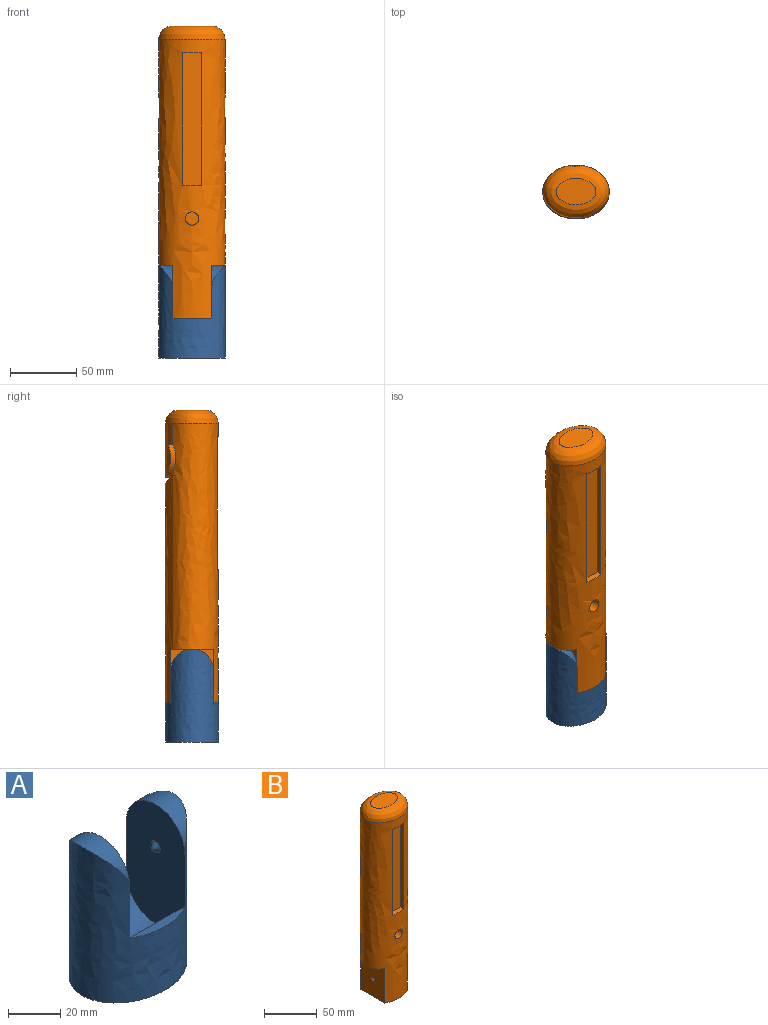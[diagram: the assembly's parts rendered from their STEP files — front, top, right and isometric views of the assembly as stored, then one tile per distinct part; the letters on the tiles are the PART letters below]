
ASSEMBLY  parts=2 mates=1
PART A: 13 faces, bbox 50x40x70 mm
  f0: extruded ~70x50mm, area 7085.2mm2, adj f1,f2,f3,f4,f5,f11,f12
  f1: plane 56x32mm, normal (1,0,0), area 1552.6mm2, adj f0,f6,f8,f12
  f2: plane 56x32mm, normal (-1,0,0), area 1552.6mm2, adj f0,f6,f10,f11
  f3: plane 30x4mm, normal (0,0,1), area 81.8mm2, adj f0,f6
  f4: plane 30x4mm, normal (0,0,1), area 81.8mm2, adj f0,f6
  f5: plane 50x40mm, normal (0,0,-1), area 1570.8mm2, adj f0
  f6: cylinder r=16mm len=32mm, axis (-1,0,0), area 1508mm2, adj f1,f2,f3,f4
  f7: plane 1x1mm, normal (1,0,0), area 0.8mm2, adj f8
  f8: cone r=0.5mm half-angle=45deg, axis (-1,0,0), area 26.7mm2, adj f1,f7
  f9: plane 1x1mm, normal (-1,0,0), area 0.8mm2, adj f10
  f10: cone r=0.5mm half-angle=45deg, axis (1,0,0), area 26.7mm2, adj f2,f9
  f11: cylinder r=16mm len=32mm, axis (-1,0,0), area 267.1mm2, adj f0,f2
  f12: cylinder r=16mm len=32mm, axis (1,0,0), area 267.1mm2, adj f0,f1
PART B: 30 faces, bbox 50.2x40.2x220.2 mm
  f0: extruded ~210x49.99mm, area 23499.3mm2, adj f1,f3,f4,f5,f6,f7,f8,f9
  f1: extruded ~40.83x32.29mm, area 960.6mm2, adj f0,f8,f21,f22,f23,f28
  f2: plane 30x20.01mm, normal (0,0,1), area 466.8mm2, adj f8
  f3: plane 32x10mm, normal (0,0,-1), area 223.6mm2, adj f0,f6
  f4: plane 32x10mm, normal (0,0,-1), area 223.6mm2, adj f0,f7
  f5: plane 40x30mm, normal (0,0,-1), area 1123.5mm2, adj f0,f6,f7
  f6: plane 40x32mm, normal (-1,0,0), area 1260.4mm2, adj f0,f3,f5,f19
  f7: plane 40x32mm, normal (1,0,0), area 1260.4mm2, adj f0,f4,f5,f17
  f8: bspline ~50.01x40.01mm, area 1847.2mm2, adj f0,f1,f2,f27,f28,f29
  f9: plane 100x4.08mm, normal (-1,0,0), area 407.9mm2, adj f0,f10,f12,f13
  f10: plane 15x5mm, normal (0,0,-1), area 70.4mm2, adj f0,f9,f11,f13
  f11: plane 100x4.08mm, normal (1,0,0), area 407.9mm2, adj f0,f10,f12,f13
  f12: plane 15x5mm, normal (0,0,1), area 70.4mm2, adj f0,f9,f11,f13
  f13: plane 100x15mm, normal (0,-1,0), area 1500mm2, adj f9,f10,f11,f12
  f14: cylinder r=5mm len=10mm, axis (0,-1,0), area 314.2mm2, adj f0,f15
  f15: plane 10x10mm, normal (0,-1,0), area 78.5mm2, adj f14
  f16: plane 1x1mm, normal (1,0,0), area 0.8mm2, adj f17
  f17: cone r=0.5mm half-angle=45deg, axis (1,0,0), area 26.7mm2, adj f7,f16
  f18: plane 1x1mm, normal (-1,0,0), area 0.8mm2, adj f19
  f19: cone r=0.5mm half-angle=45deg, axis (-1,0,0), area 26.7mm2, adj f6,f18
  f20: plane 7.9x0.93mm, normal (-0.3,0,-0.95), area 7.7mm2, adj f0,f24,f26,f27
  f21: cylinder r=6.25mm len=8mm, axis (0,-1,0), area 46.1mm2, adj f1,f22,f26,f28
  f22: cylinder r=15mm len=30mm, axis (0,-1,0), area 479.7mm2, adj f1,f21,f23,f26
  f23: plane 6.16x5.92mm, normal (0,0,-1), area 26.9mm2, adj f1,f22,f25,f26
  f24: cylinder r=20mm len=18.7mm, axis (0,-1,0), area 105.3mm2, adj f0,f20,f26
  f25: cylinder r=20mm len=39.98mm, axis (0,-1,0), area 276.6mm2, adj f0,f23,f26
  f26: plane 50x39.98mm, normal (0,1,0), area 524.9mm2, adj f0,f20,f21,f22,f23,f24,f25,f27
  f27: plane 10.16x8.05mm, normal (-1,0,0), area 77.7mm2, adj f0,f8,f20,f26,f29
  f28: plane 10.13x8.03mm, normal (1,0,0), area 77.8mm2, adj f1,f8,f21,f26,f29
  f29: plane 7.1x5.01mm, normal (0,0,-1), area 35.3mm2, adj f8,f26,f27,f28
PLACE A t=(34.47,-49.65,-91.48)mm
PLACE B t=(53.59,-65.42,-61.48)mm
MATE pin_slot A.f8 <-> B.f17  axis (1,0,0) through (-12.01,-8.98,-41.48)mm
